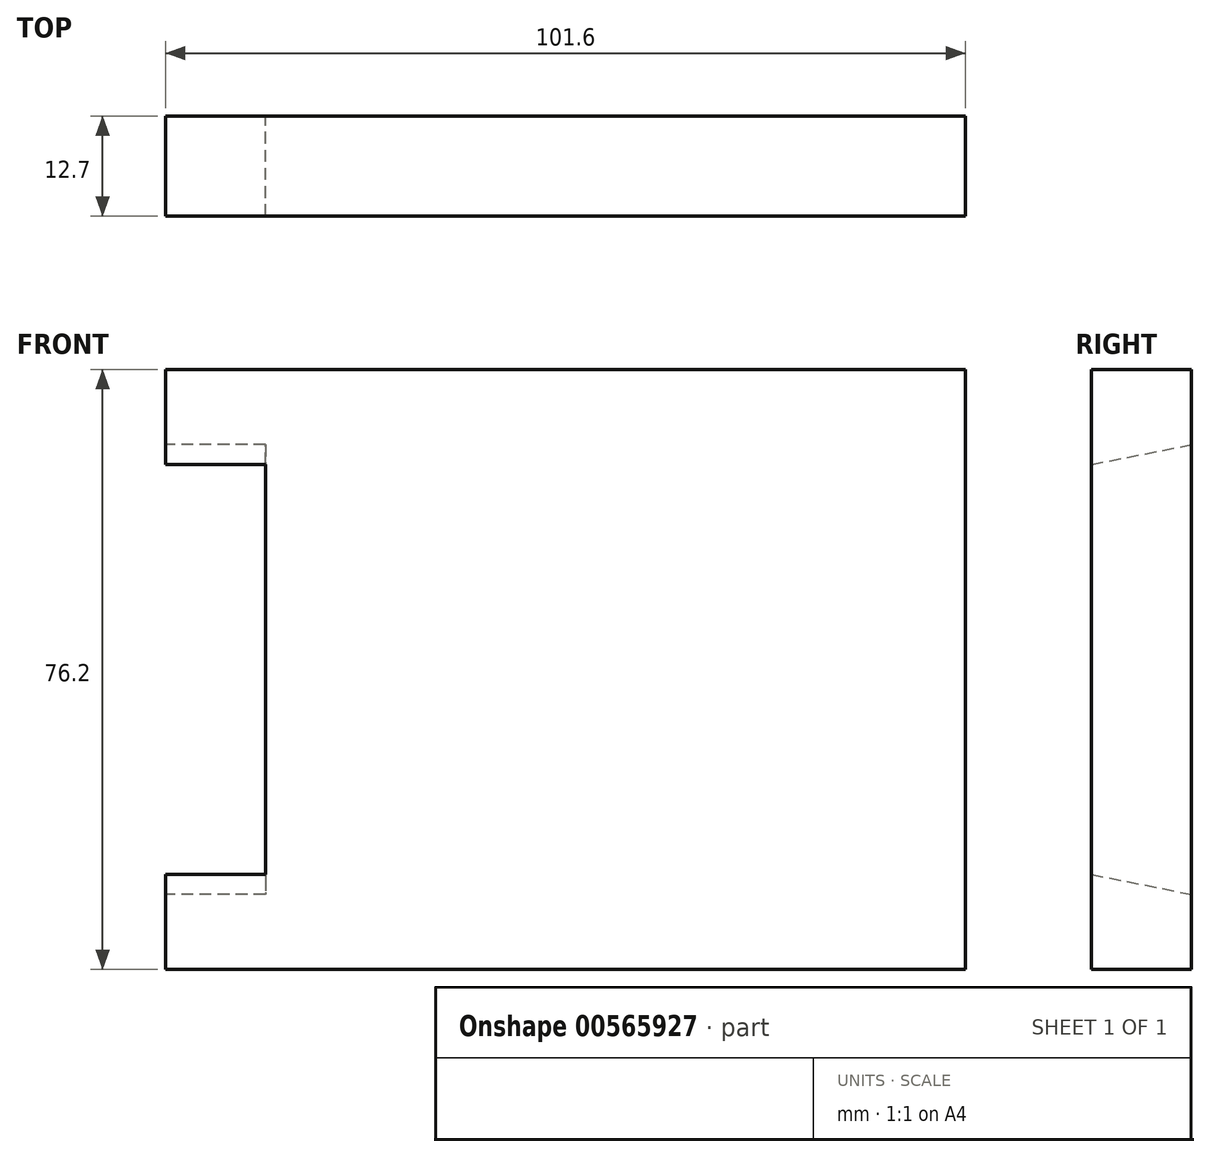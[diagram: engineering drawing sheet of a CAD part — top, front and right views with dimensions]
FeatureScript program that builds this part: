
annotation { "Feature Type Name" : "Feature", "Feature Type Description" : "" }
export const myFeature = defineFeature(function(context is Context, id is Id, definition is map)
    precondition{}
    {
        {
            var Q0;
            Q0=qCreatedBy(makeId("Right.planeOp"),FACE);
            var sketch = newSketch(context, id + "F0", { "sketchPlane" : qUnion([Q0])});
            skLineSegment(sketch, "E0.bottom", {"start": v(-6.35, 38.1) * mm, "end": v(6.35, 38.1) * mm});
            skLineSegment(sketch, "E0.top", {"start": v(-6.35, -38.1) * mm, "end": v(6.35, -38.1) * mm});
            skLineSegment(sketch, "E0.left", {"start": v(-6.35, 38.1) * mm, "end": v(-6.35, -38.1) * mm});
            skLineSegment(sketch, "E0.right", {"start": v(6.35, 38.1) * mm, "end": v(6.35, -38.1) * mm});
            skLineSegment(sketch, "E1", {"start": v(-6.35, 38.1) * mm, "end": v(6.35, -38.1) * mm, "construction": true});
            skSolve(sketch);
        }
        {
            var Q0;
            Q0 = qSketchRegion(id + "F0", true);
            extrude(context, id + "F1", {"entities" : qUnion([Q0]), "endBound" : BoundingType.SYMMETRIC, "depth" : 101.6 * mm, "offsetDistance" : 25.4 * mm});
        }
        {
            var Q0;
            Q0=makeQuery(id+"F1.opExtrude","CAP_FACE",FACE,{"disambiguationData":[OSD([sQuery(id+"F0.wireOp",EDGE,"E0.bottom"),sQuery(id+"F0.wireOp",EDGE,"E0.top"),sQuery(id+"F0.wireOp",EDGE,"E0.left"),sQuery(id+"F0.wireOp",EDGE,"E0.right")])],"isStart":true});
            var sketch = newSketch(context, id + "F2", { "sketchPlane" : qUnion([Q0])});
            skLineSegment(sketch, "E2", {"start": v(6.35, 26.04) * mm, "end": v(-6.35, 28.58) * mm});
            skLineSegment(sketch, "E3", {"start": v(-6.35, 28.58) * mm, "end": v(14.26, 28.58) * mm, "construction": true});
            skLineSegment(sketch, "E4.MirrorCS", {"start": v(6.35, -26.04) * mm, "end": v(-6.35, -28.58) * mm});
            skLineSegment(sketch, "E5", {"start": v(-6.35, 28.58) * mm, "end": v(-6.35, -28.58) * mm});
            skLineSegment(sketch, "E6", {"start": v(6.35, -26.04) * mm, "end": v(6.35, 26.04) * mm});
            skSolve(sketch);
        }
        {
            var Q0;
            Q0 = qSketchRegion(id + "F2", true);
            extrude(context, id + "F3", {"entities" : qUnion([Q0]), "operationType" : NewBodyOperationType.REMOVE, "oppositeDirection" : true, "depth" : 12.7 * mm, "offsetDistance" : 25.4 * mm});
        }
    });
